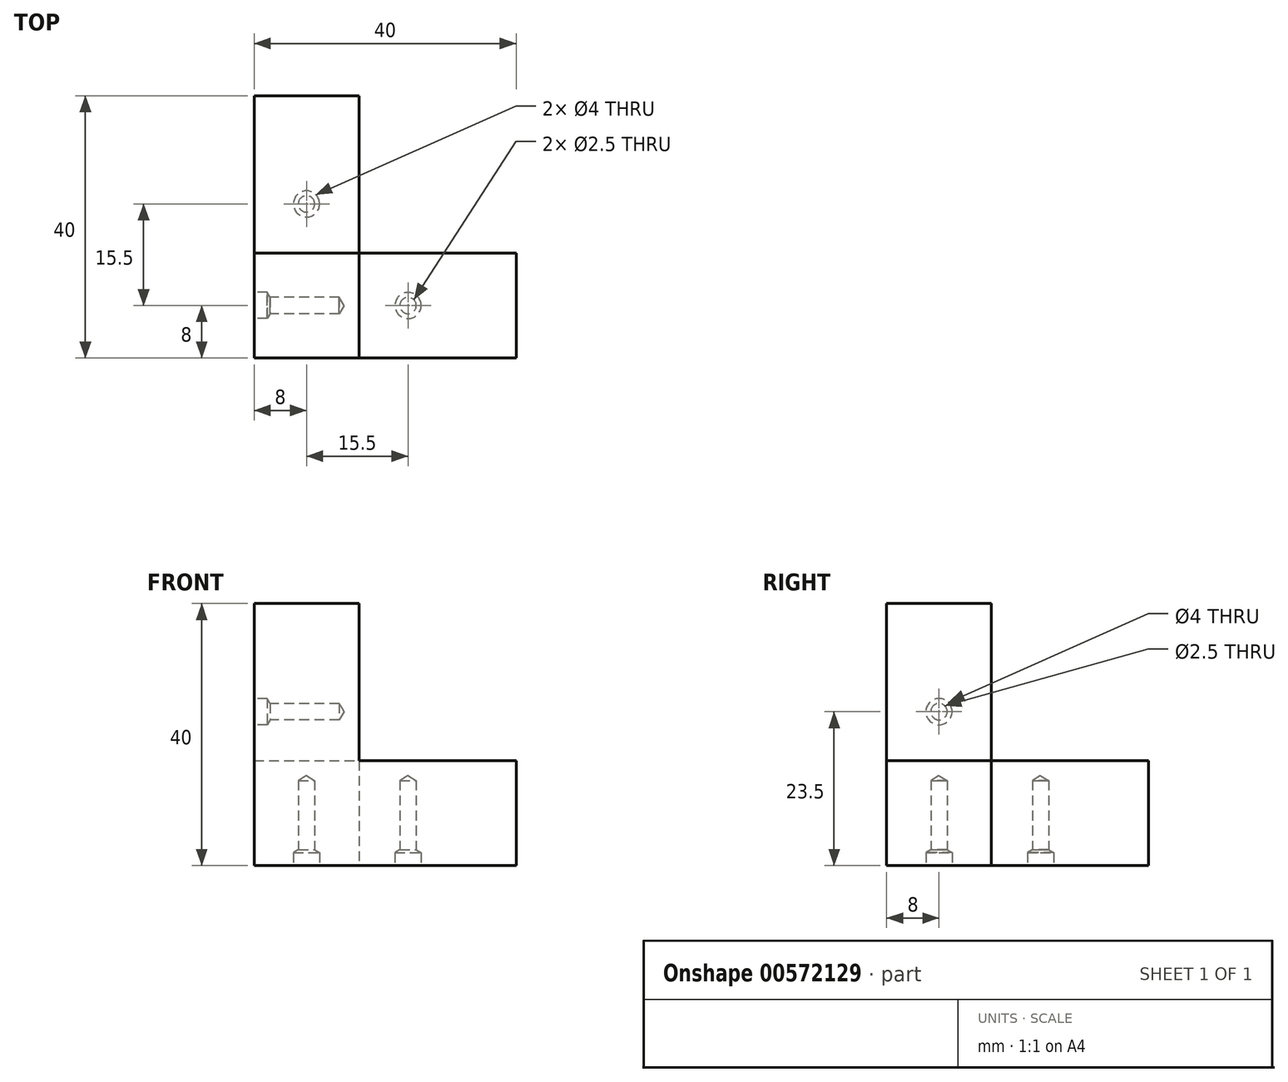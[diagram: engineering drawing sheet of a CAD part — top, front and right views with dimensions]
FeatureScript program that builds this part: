
annotation { "Feature Type Name" : "Feature", "Feature Type Description" : "" }
export const myFeature = defineFeature(function(context is Context, id is Id, definition is map)
    precondition{}
    {
        {
            var Q0;
            Q0=qCreatedBy(makeId("Right.planeOp"),FACE);
            cPlane(context, id + "F0", {"entities" : qUnion([Q0]), "cplaneType" : CPlaneType.OFFSET, "offset" : 17.5 * mm, "oppositeDirection" : true, "width" : 150 * mm, "height" : 150 * mm});
        }
        {
            var Q0;
            Q0=qCreatedBy(makeId("Top.planeOp"),FACE);
            cPlane(context, id + "F1", {"entities" : qUnion([Q0]), "cplaneType" : CPlaneType.OFFSET, "offset" : 17.5 * mm, "oppositeDirection" : true, "width" : 150 * mm, "height" : 150 * mm});
        }
        {
            var Q0;
            Q0=qCreatedBy(makeId("Front.planeOp"),FACE);
            cPlane(context, id + "F2", {"entities" : qUnion([Q0]), "cplaneType" : CPlaneType.OFFSET, "offset" : 17.5 * mm, "width" : 150 * mm, "height" : 150 * mm});
        }
        {
            var Q0;
            Q0=qCreatedBy(id+"F2.planeOp",FACE);
            var sketch = newSketch(context, id + "F3", { "sketchPlane" : qUnion([Q0])});
            skLineSegment(sketch, "E0.bottom", {"start": v(-1.5, -1.5) * mm, "end": v(-17.5, -1.5) * mm});
            skLineSegment(sketch, "E0.top", {"start": v(-1.5, -17.5) * mm, "end": v(-17.5, -17.5) * mm});
            skLineSegment(sketch, "E0.left", {"start": v(-1.5, -1.5) * mm, "end": v(-1.5, -17.5) * mm});
            skLineSegment(sketch, "E0.right", {"start": v(-17.5, -1.5) * mm, "end": v(-17.5, -17.5) * mm});
            skPoint(sketch, "E1", {"position": v(-1.5, -1.5) * mm});
            skPoint(sketch, "E2", {"position": v(0, 0) * mm});
            skSolve(sketch);
        }
        {
            var Q0;
            Q0=qCreatedBy(id+"F0.planeOp",FACE);
            var sketch = newSketch(context, id + "F4", { "sketchPlane" : qUnion([Q0])});
            skLineSegment(sketch, "E3.bottom", {"start": v(-1.5, -1.5) * mm, "end": v(-17.5, -1.5) * mm});
            skLineSegment(sketch, "E3.top", {"start": v(-1.5, -17.5) * mm, "end": v(-17.5, -17.5) * mm});
            skLineSegment(sketch, "E3.left", {"start": v(-1.5, -1.5) * mm, "end": v(-1.5, -17.5) * mm});
            skLineSegment(sketch, "E3.right", {"start": v(-17.5, -1.5) * mm, "end": v(-17.5, -17.5) * mm});
            skPoint(sketch, "E4", {"position": v(0, 0) * mm});
            skPoint(sketch, "E5", {"position": v(-1.5, -1.5) * mm});
            skPoint(sketch, "E6", {"position": v(-9.5, 6) * mm});
            skSolve(sketch);
        }
        {
            var Q0;
            Q0=qCreatedBy(id+"F1.planeOp",FACE);
            var sketch = newSketch(context, id + "F5", { "sketchPlane" : qUnion([Q0])});
            skLineSegment(sketch, "E7.bottom", {"start": v(-1.5, -1.5) * mm, "end": v(-17.5, -1.5) * mm});
            skLineSegment(sketch, "E7.top", {"start": v(-1.5, -17.5) * mm, "end": v(-17.5, -17.5) * mm});
            skLineSegment(sketch, "E7.left", {"start": v(-1.5, -1.5) * mm, "end": v(-1.5, -17.5) * mm});
            skLineSegment(sketch, "E7.right", {"start": v(-17.5, -1.5) * mm, "end": v(-17.5, -17.5) * mm});
            skPoint(sketch, "E8", {"position": v(-1.5, -1.5) * mm});
            skPoint(sketch, "E9", {"position": v(0, 0) * mm});
            skPoint(sketch, "E10", {"position": v(6, -9.5) * mm});
            skPoint(sketch, "E11", {"position": v(-9.5, 6) * mm});
            skSolve(sketch);
        }
        {
            var Q0;
            Q0=makeQuery(id+"F3.imprint","IMPRINT",FACE,{"disambiguationData":[TD([[makeQuery(id+"F3.imprint","IMPRINT",EDGE,{"derivedFrom":sQuery(id+"F3.wireOp",EDGE,"E0.bottom")}),1.0]])]});
            extrude(context, id + "F6", {"entities" : qUnion([Q0]), "oppositeDirection" : true, "depth" : 40 * mm, "offsetDistance" : 25 * mm});
        }
        {
            var Q0;
            Q0=makeQuery(id+"F4.imprint","IMPRINT",FACE,{"disambiguationData":[TD([[makeQuery(id+"F4.imprint","IMPRINT",EDGE,{"derivedFrom":sQuery(id+"F4.wireOp",EDGE,"E3.bottom")}),1.0]])]});
            extrude(context, id + "F7", {"entities" : qUnion([Q0]), "operationType" : NewBodyOperationType.ADD, "depth" : 40 * mm, "offsetDistance" : 25 * mm});
        }
        {
            var Q0;
            Q0=makeQuery(id+"F5.imprint","IMPRINT",FACE,{"disambiguationData":[TD([[makeQuery(id+"F5.imprint","IMPRINT",EDGE,{"derivedFrom":sQuery(id+"F5.wireOp",EDGE,"E7.bottom")}),1.0]])]});
            extrude(context, id + "F8", {"entities" : qUnion([Q0]), "operationType" : NewBodyOperationType.ADD, "depth" : 40 * mm, "offsetDistance" : 25 * mm});
        }
        {
            var Q0;
            Q0=sQuery(id+"F5.wireOp",VERTEX,"E10");
            var Q1;
            Q1=makeQuery(id+"F6.opExtrude","SWEPT_BODY",BODY,{"disambiguationData":[OSD([sQuery(id+"F3.wireOp",EDGE,"E0.bottom"),sQuery(id+"F3.wireOp",EDGE,"E0.top"),sQuery(id+"F3.wireOp",EDGE,"E0.left"),sQuery(id+"F3.wireOp",EDGE,"E0.right")])]});
            hole(context, id + "F9", {"style" : HoleStyle.SIMPLE, "endStyle" : HoleEndStyle.BLIND, "oppositeDirection" : true, "holeDiameter" : 2.5 * mm, "holeDepth" : 13 * mm, "isTappedThrough" : true, "tappedDepth" : 12 * mm, "tapClearance" : 3, "locations" : qUnion([Q0]), "scope" : qUnion([Q1])});
        }
        {
            var Q0;
            Q0=sQuery(id+"F5.wireOp",VERTEX,"E10");
            var Q1;
            Q1=makeQuery(id+"F6.opExtrude","SWEPT_BODY",BODY,{"disambiguationData":[OSD([sQuery(id+"F3.wireOp",EDGE,"E0.bottom"),sQuery(id+"F3.wireOp",EDGE,"E0.top"),sQuery(id+"F3.wireOp",EDGE,"E0.left"),sQuery(id+"F3.wireOp",EDGE,"E0.right")])]});
            hole(context, id + "F10", {"style" : HoleStyle.SIMPLE, "endStyle" : HoleEndStyle.BLIND, "oppositeDirection" : true, "holeDiameter" : 4 * mm, "holeDepth" : 2 * mm, "isTappedThrough" : true, "tappedDepth" : 12 * mm, "tapClearance" : 3, "locations" : qUnion([Q0]), "scope" : qUnion([Q1])});
        }
        {
            var Q0;
            Q0=sQuery(id+"F5.wireOp",VERTEX,"E11");
            var Q1;
            Q1=makeQuery(id+"F6.opExtrude","SWEPT_BODY",BODY,{"disambiguationData":[OSD([sQuery(id+"F3.wireOp",EDGE,"E0.bottom"),sQuery(id+"F3.wireOp",EDGE,"E0.top"),sQuery(id+"F3.wireOp",EDGE,"E0.left"),sQuery(id+"F3.wireOp",EDGE,"E0.right")])]});
            hole(context, id + "F11", {"style" : HoleStyle.SIMPLE, "endStyle" : HoleEndStyle.BLIND, "oppositeDirection" : true, "holeDiameter" : 2.5 * mm, "holeDepth" : 13 * mm, "isTappedThrough" : true, "tappedDepth" : 12 * mm, "tapClearance" : 3, "locations" : qUnion([Q0]), "scope" : qUnion([Q1])});
        }
        {
            var Q0;
            Q0=sQuery(id+"F5.wireOp",VERTEX,"E11");
            var Q1;
            Q1=makeQuery(id+"F6.opExtrude","SWEPT_BODY",BODY,{"disambiguationData":[OSD([sQuery(id+"F3.wireOp",EDGE,"E0.bottom"),sQuery(id+"F3.wireOp",EDGE,"E0.top"),sQuery(id+"F3.wireOp",EDGE,"E0.left"),sQuery(id+"F3.wireOp",EDGE,"E0.right")])]});
            hole(context, id + "F12", {"style" : HoleStyle.SIMPLE, "endStyle" : HoleEndStyle.BLIND, "oppositeDirection" : true, "holeDiameter" : 4 * mm, "holeDepth" : 2 * mm, "isTappedThrough" : true, "tappedDepth" : 12 * mm, "tapClearance" : 3, "locations" : qUnion([Q0]), "scope" : qUnion([Q1])});
        }
        {
            var Q0;
            Q0=sQuery(id+"F4.wireOp",VERTEX,"E6");
            var Q1;
            Q1=makeQuery(id+"F6.opExtrude","SWEPT_BODY",BODY,{"disambiguationData":[OSD([sQuery(id+"F3.wireOp",EDGE,"E0.bottom"),sQuery(id+"F3.wireOp",EDGE,"E0.top"),sQuery(id+"F3.wireOp",EDGE,"E0.left"),sQuery(id+"F3.wireOp",EDGE,"E0.right")])]});
            hole(context, id + "F13", {"style" : HoleStyle.SIMPLE, "endStyle" : HoleEndStyle.BLIND, "oppositeDirection" : true, "holeDiameter" : 2.5 * mm, "holeDepth" : 13 * mm, "isTappedThrough" : true, "tappedDepth" : 12 * mm, "tapClearance" : 3, "locations" : qUnion([Q0]), "scope" : qUnion([Q1])});
        }
        {
            var Q0;
            Q0=sQuery(id+"F4.wireOp",VERTEX,"E6");
            var Q1;
            Q1=makeQuery(id+"F6.opExtrude","SWEPT_BODY",BODY,{"disambiguationData":[OSD([sQuery(id+"F3.wireOp",EDGE,"E0.bottom"),sQuery(id+"F3.wireOp",EDGE,"E0.top"),sQuery(id+"F3.wireOp",EDGE,"E0.left"),sQuery(id+"F3.wireOp",EDGE,"E0.right")])]});
            hole(context, id + "F14", {"style" : HoleStyle.SIMPLE, "endStyle" : HoleEndStyle.BLIND, "oppositeDirection" : true, "holeDiameter" : 4 * mm, "holeDepth" : 2 * mm, "isTappedThrough" : true, "tappedDepth" : 12 * mm, "tapClearance" : 3, "locations" : qUnion([Q0]), "scope" : qUnion([Q1])});
        }
    });
